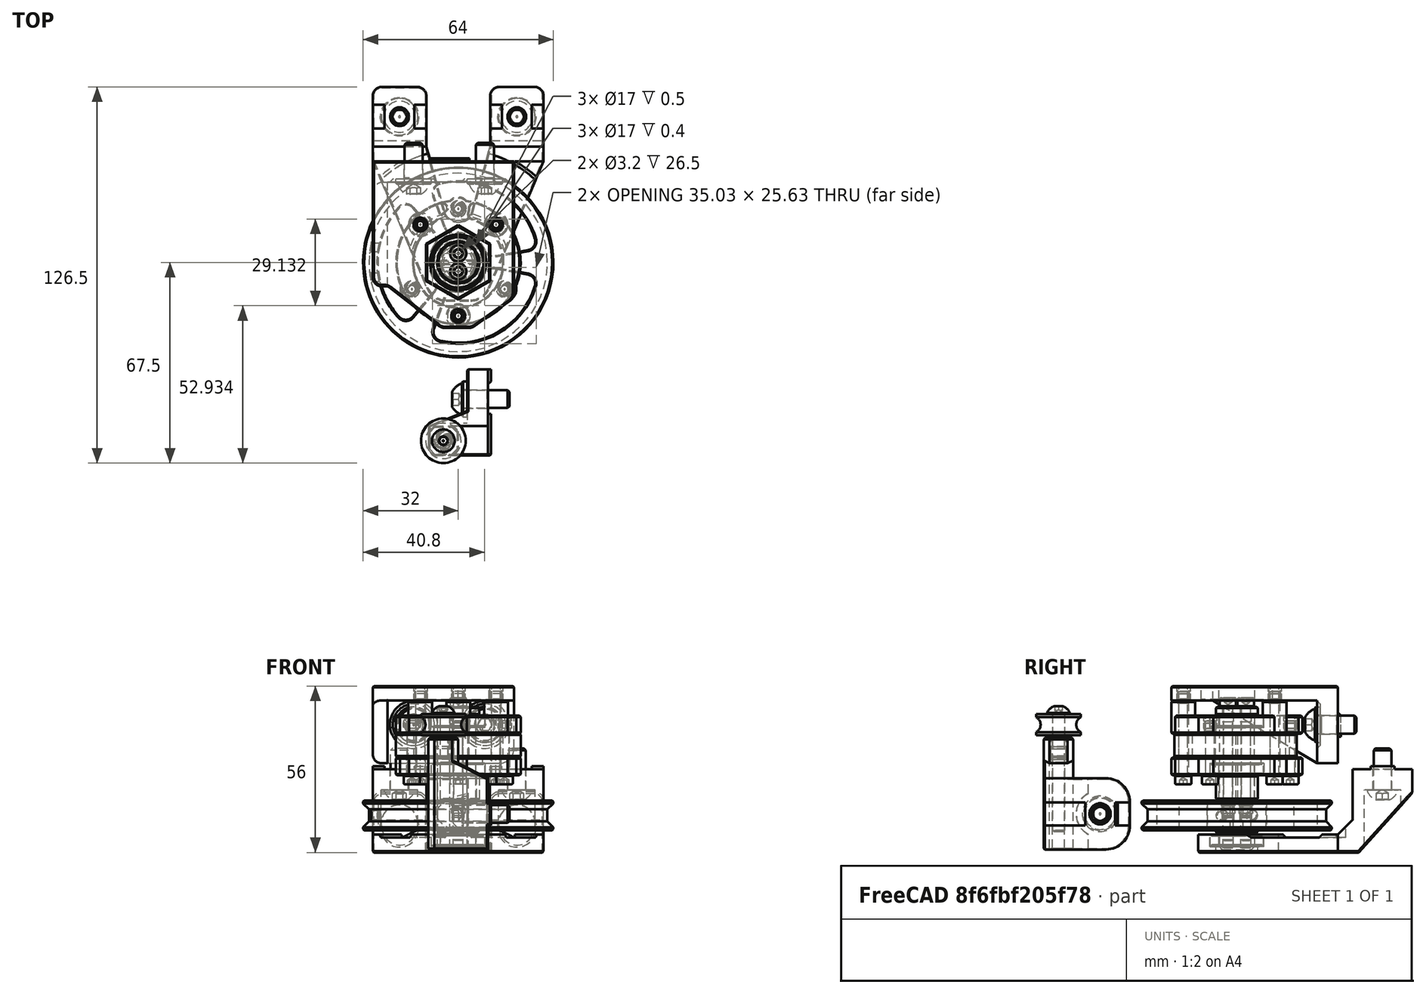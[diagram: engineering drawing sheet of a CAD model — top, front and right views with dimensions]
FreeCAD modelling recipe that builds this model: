
FCSTD DOCUMENT  (FreeCAD 0.19R24291 (Git))
Label: counter-weight-spring-box-assembly
License: Other
LicenseURL: GPL3
objects: Part::FeaturePython×26, Part::Feature×15, PartDesign::CoordinateSystem×2, App::Part×2
note: 43 computed .brp shape members not serialized (recipe doc carries the construction recipe); baked Part::Feature solids carry a one-line shape summary decoded from their .brp

FEATURE [Part::Feature] Chamfer001001  label="bearing-6701ZZ1"
  Placement = pos=(0,0,-2) rot=(0,0,1;0rad)
  shape: bbox 18 x 18 x 4 mm, 20 faces (baked)
FEATURE [Part::Feature] Body001001001002003011001005  label="cw-mid-plate"
  Placement = pos=(0,0,-2) rot=(0,0,1;0rad)
  shape: bbox 42 x 41.91 x 12.4 mm, 62 faces (baked)
FEATURE [Part::Feature] Body003002  label="cw-axis"
  Placement = pos=(0,0,21) rot=(0.707107,-0.707107,0;3.14159rad)
  shape: bbox 14.1 x 14.1 x 31.5 mm, 25 faces (baked)
FEATURE [Part::Feature] Body001001001002003011001002001  label="cw-front-plate"
  Placement = pos=(0,0,-2) rot=(0,0,1;0rad)
  shape: bbox 42 x 44 x 6 mm, 67 faces (baked)
FEATURE [Part::Feature] Body001001001002003011001003001  label="cw-back-plate"
  Placement = pos=(0,0,-2) rot=(0,0,1;0rad)
  shape: bbox 42 x 44 x 11 mm, 69 faces (baked)
FEATURE [Part::Feature] Chamfer003068012002063001  label="bearing-6701ZZ2"
  Placement = pos=(0,0,14) rot=(0,0,1;0rad)
  shape: bbox 18 x 18 x 4 mm, 20 faces (baked)
FEATURE [Part::Feature] Body001001001002003011001004001  label="cw-spacer"
  Placement = pos=(0,0,-2) rot=(0,0,1;0rad)
  shape: bbox 14.1 x 14.1 x 8.35 mm, 6 faces (baked)
FEATURE [Part::Feature] Chamfer003068012002073001  label="bearing-6701ZZ"
  Placement = pos=(0,0,-26) rot=(0,0,1;0rad)
  shape: bbox 18 x 18 x 4 mm, 20 faces (baked)
FEATURE [Part::Feature] Chamfer003068012002090001  label="cw-front-mounter"
  shape: bbox 57.46 x 72 x 29 mm, 102 faces (baked)
FEATURE [Part::Feature] Chamfer003068012002102001  label="cw-back-mounter"
  Placement = pos=(0,0,-20) rot=(0,0,1;0rad)
  shape: bbox 47.46 x 57 x 26 mm, 78 faces (baked)
FEATURE [Part::Feature] Body001001001002003011001004002  label="cw-pulley-r30"
  Placement = pos=(1e-15,0,-10.5) rot=(0,1,0;3.14159rad)
  shape: bbox 64 x 64 x 16.5 mm, 104 faces (baked)
FEATURE [Part::FeaturePython] HeatSet  label="M3x4-HeatSet"  # WARN: FeaturePython — macro-defined, semantics opaque (R4)
  Placement = pos=(-12.7279,12.7279,28) rot=(0,0,1;0rad)
  baseObject = -> Chamfer003068012002102001 [Edge160]
  diameter = 2
  invert = false
  leftHanded = false
  offset = 0
FEATURE [Part::FeaturePython] HeatSet001  label="M3x4-HeatSet001"  # WARN: FeaturePython — macro-defined, semantics opaque (R4)
  Placement = pos=(0,-18,28) rot=(0,0,1;0rad)
  baseObject = -> Chamfer003068012002102001 [Edge162]
  diameter = 2
  invert = false
  leftHanded = false
  offset = 0
FEATURE [Part::FeaturePython] HeatSet002  label="M3x4-HeatSet002"  # WARN: FeaturePython — macro-defined, semantics opaque (R4)
  Placement = pos=(12.7279,12.7279,28) rot=(0,0,1;0rad)
  baseObject = -> Chamfer003068012002102001 [Edge161]
  diameter = 2
  invert = false
  leftHanded = false
  offset = 0
FEATURE [Part::FeaturePython] HeatSet004  label="M3x4-HeatSet003"  # WARN: FeaturePython — macro-defined, semantics opaque (R4)
  Placement = pos=(15.5885,-9,18) rot=(0,0,1;0rad)
  baseObject = -> Body001001001002003011001003001 [Edge19]
  diameter = 2
  invert = false
  leftHanded = false
  offset = 0
FEATURE [Part::FeaturePython] HeatSet005  label="M3x4-HeatSet004"  # WARN: FeaturePython — macro-defined, semantics opaque (R4)
  Placement = pos=(-15.5885,-9,18) rot=(0,0,1;0rad)
  baseObject = -> Body001001001002003011001003001 [Edge17]
  diameter = 2
  invert = false
  leftHanded = false
  offset = 0
FEATURE [Part::FeaturePython] HeatSet006  label="M3x4-HeatSet005"  # WARN: FeaturePython — macro-defined, semantics opaque (R4)
  Placement = pos=(1.1e-15,18,18) rot=(0,0,1;0rad)
  baseObject = -> Body001001001002003011001003001 [Edge20]
  diameter = 2
  invert = false
  leftHanded = false
  offset = 0
FEATURE [Part::FeaturePython] HeatSet007  label="M3x4-HeatSet006"  # WARN: FeaturePython — macro-defined, semantics opaque (R4)
  Placement = pos=(0,-3,-10.5) rot=(0,0,1;0rad)
  baseObject = -> Body001001001002003011001004002 [Edge68]
  diameter = 2
  invert = false
  leftHanded = false
  offset = 0
FEATURE [Part::FeaturePython] HeatSet008  label="M3x4-HeatSet007"  # WARN: FeaturePython — macro-defined, semantics opaque (R4)
  Placement = pos=(2e-15,3,-10.5) rot=(0,0,1;0rad)
  baseObject = -> Body001001001002003011001004002 [Edge69]
  diameter = 2
  invert = false
  leftHanded = false
  offset = 0
FEATURE [Part::FeaturePython] Screw  label="M3x20-Screw"  # Fasteners workbench fastener (typed FeaturePython)
  Placement = pos=(15.5885,-9,-2) rot=(1,0,0;3.14159rad)
  baseObject = -> Body001001001002003011001002001 [Edge49]
  diameter = 4
  invert = false
  leftHanded = false
  length = 7
  lengthCustom = 20
  matchOuter = true
  offset = 0
  thread = false
  type = 34
FEATURE [Part::FeaturePython] Screw001  label="M3x20-Screw003"  # Fasteners workbench fastener (typed FeaturePython)
  Placement = pos=(-15.5885,-9,-2) rot=(1,0,0;3.14159rad)
  baseObject = -> Body001001001002003011001002001 [Edge48]
  diameter = 4
  invert = false
  leftHanded = false
  length = 7
  lengthCustom = 20
  matchOuter = true
  offset = 0
  thread = false
  type = 34
FEATURE [Part::FeaturePython] Screw002  label="M3x20-Screw004"  # Fasteners workbench fastener (typed FeaturePython)
  Placement = pos=(1e-15,18,-2) rot=(1,0,0;3.14159rad)
  baseObject = -> Body001001001002003011001002001 [Edge51]
  diameter = 4
  invert = false
  leftHanded = false
  length = 7
  lengthCustom = 20
  matchOuter = true
  offset = 0
  thread = false
  type = 34
FEATURE [Part::FeaturePython] Screw003  label="M3x30-Screw"  # Fasteners workbench fastener (typed FeaturePython)
  Placement = pos=(12.7279,12.7279,-2) rot=(1,0,0;3.14159rad)
  baseObject = -> Body001001001002003011001002001 [Edge47]
  diameter = 4
  invert = false
  leftHanded = false
  length = 9
  lengthCustom = 30
  matchOuter = true
  offset = 0
  thread = false
  type = 34
FEATURE [Part::FeaturePython] Screw004  label="M3x30-Screw003"  # Fasteners workbench fastener (typed FeaturePython)
  Placement = pos=(-12.7279,12.7279,-2) rot=(1,0,0;3.14159rad)
  baseObject = -> Body001001001002003011001002001 [Edge46]
  diameter = 4
  invert = false
  leftHanded = false
  length = 9
  lengthCustom = 30
  matchOuter = true
  offset = 0
  thread = false
  type = 34
FEATURE [Part::FeaturePython] Screw005  label="M3x30-Screw004"  # Fasteners workbench fastener (typed FeaturePython)
  Placement = pos=(-1.2155e-11,-18,-2) rot=(1,0,0;3.14159rad)
  baseObject = -> Body001001001002003011001002001 [Edge50]
  diameter = 4
  invert = false
  leftHanded = false
  length = 9
  lengthCustom = 30
  matchOuter = true
  offset = 0
  thread = false
  type = 34
FEATURE [Part::FeaturePython] Screw006  label="M3x45-Screw"  # Fasteners workbench fastener (typed FeaturePython)
  Placement = pos=(-1e-15,3,21) rot=(0,0,1;0rad)
  baseObject = -> Body003002 [Edge7]
  diameter = 4
  invert = true
  leftHanded = false
  length = 10
  lengthCustom = 45
  matchOuter = true
  offset = 0
  thread = false
  type = 34
FEATURE [Part::FeaturePython] Screw007  label="M3x45-Screw001"  # Fasteners workbench fastener (typed FeaturePython)
  Placement = pos=(1e-15,-3,21) rot=(0,0,1;0rad)
  baseObject = -> Body003002 [Edge8]
  diameter = 4
  invert = true
  leftHanded = false
  length = 10
  lengthCustom = 45
  matchOuter = true
  offset = 0
  thread = false
  type = 34
FEATURE [Part::FeaturePython] Washer  label="M6-Washer"  # Fasteners workbench fastener (typed FeaturePython)
  Placement = pos=(9,28,15) rot=(1,0,0;1.5708rad)
  baseObject = -> Chamfer003068012002102001 [Edge163]
  diameter = 2
  invert = true
  leftHanded = false
  matchOuter = true
  offset = 0
  type = 4
FEATURE [Part::FeaturePython] Washer001  label="M6-Washer001"  # Fasteners workbench fastener (typed FeaturePython)
  Placement = pos=(-15,28,15) rot=(1,0,0;1.5708rad)
  baseObject = -> Chamfer003068012002102001 [Edge97]
  diameter = 2
  invert = true
  leftHanded = false
  matchOuter = true
  offset = 0
  type = 4
FEATURE [Part::FeaturePython] Screw008  label="M6x14-Screw"  # Fasteners workbench fastener (typed FeaturePython)
  Placement = pos=(9,26.2,15) rot=(1,0,0;1.5708rad)
  baseObject = -> Washer [Edge1]
  diameter = 4
  invert = false
  leftHanded = false
  length = 2
  lengthCustom = 14
  matchOuter = true
  offset = 0
  thread = false
  type = 40
FEATURE [Part::FeaturePython] Screw009  label="M6x14-Screw001"  # Fasteners workbench fastener (typed FeaturePython)
  Placement = pos=(-15,26.2,15) rot=(1,0,0;1.5708rad)
  baseObject = -> Washer001 [Edge1]
  diameter = 4
  invert = false
  leftHanded = false
  length = 2
  lengthCustom = 14
  matchOuter = true
  offset = 0
  thread = false
  type = 40
FEATURE [Part::FeaturePython] Screw010  label="M6x14-Screw002"  # Fasteners workbench fastener (typed FeaturePython)
  Placement = pos=(-19.73,49,-7) rot=(1,0,0;3.14159rad)
  baseObject = -> Chamfer003068012002090001 [Edge194]
  diameter = 4
  invert = true
  leftHanded = false
  length = 2
  lengthCustom = 14
  matchOuter = true
  offset = 0
  thread = false
  type = 40
FEATURE [Part::FeaturePython] Screw011  label="M6x14-Screw003"  # Fasteners workbench fastener (typed FeaturePython)
  Placement = pos=(19.73,49,-7) rot=(1,0,0;3.14159rad)
  baseObject = -> Chamfer003068012002090001 [Edge254]
  diameter = 4
  invert = true
  leftHanded = false
  length = 2
  lengthCustom = 14
  matchOuter = true
  offset = 0
  thread = false
  type = 40
FEATURE [PartDesign::CoordinateSystem] LCS_counter_spring_box  label="LCS_counter-spring-box"
  AttacherType = Attacher::AttachEngine3D
FEATURE [App::Part] Part  label="counter-weight-sprintg-box"
  Group = -> [Body001001001002003011001004002,Chamfer001001,Body001001001002003011001005,Body003002,Body001001001002003011001002001,Body001001001002003011001003001,Chamfer003068012002063001,Body001001001002003011001004001,Chamfer003068012002073001,Chamfer003068012002090001,Chamfer003068012002102001,HeatSet,HeatSet001,HeatSet002,HeatSet004,HeatSet005,HeatSet006,HeatSet007,HeatSet008,Screw,Screw001,Screw002,+12 more]
  Origin = -> Origin
FEATURE [Part::Feature] Body001001001002003006001  label="counter-weight-top-arm001"
  Placement = pos=(10,-25,0) rot=(0,0,1;0rad)
  shape: bbox 21 x 29 x 37.5 mm, 69 faces (baked)
FEATURE [Part::Feature] Body001001001002003005  label="U624ZZ-bearing"
  Placement = pos=(-5,-60,15) rot=(0,1,0;1.5708rad)
  shape: bbox 15 x 15 x 7 mm, 6 faces (baked)
FEATURE [Part::Feature] Cut001021001  label="spacer-0p5mm"
  Placement = pos=(-5,-60,18.5) rot=(0,0,1;0rad)
  shape: bbox 6.3 x 6.3 x 0.5 mm, 4 faces (baked)
FEATURE [Part::Feature] Cut001020001  label="spacer-1mm"
  Placement = pos=(-5,-60,10.5) rot=(0,0,1;0rad)
  shape: bbox 6.3 x 6.3 x 1 mm, 4 faces (baked)
FEATURE [Part::FeaturePython] Screw012  label="M4x40-Screw"  # Fasteners workbench fastener (typed FeaturePython)
  Placement = pos=(-5,-60,19) rot=(0,0,1;0rad)
  baseObject = -> Cut001021001 [Edge4]
  diameter = 2
  invert = false
  leftHanded = false
  length = 10
  lengthCustom = 40
  matchOuter = true
  offset = 0
  thread = false
  type = 40
FEATURE [Part::FeaturePython] HeatSet009  label="M4-HeatSet"  # WARN: FeaturePython — macro-defined, semantics opaque (R4)
  Placement = pos=(-5,-60,10.5) rot=(0,0,1;0rad)
  baseObject = -> Body001001001002003006001 [Edge40]
  diameter = 4
  invert = false
  leftHanded = false
  offset = 0
FEATURE [Part::FeaturePython] Washer002  label="M6-Washer002"  # Fasteners workbench fastener (typed FeaturePython)
  Placement = pos=(3,-46,-15) rot=(0,-1,0;1.5708rad)
  baseObject = -> Body001001001002003006001 [Edge132]
  diameter = 2
  invert = true
  leftHanded = false
  matchOuter = true
  offset = 0
  type = 4
FEATURE [Part::FeaturePython] Screw013  label="M6x16-Screw"  # Fasteners workbench fastener (typed FeaturePython)
  Placement = pos=(1.2,-46,-15) rot=(0,-1,0;1.5708rad)
  baseObject = -> Washer002 [Edge1]
  diameter = 4
  invert = false
  leftHanded = false
  length = 3
  lengthCustom = 16
  matchOuter = true
  offset = 0
  thread = false
  type = 40
FEATURE [PartDesign::CoordinateSystem] LCS_counter_weight_top_arm  label="LCS_counter-weight-top-arm"
  AttacherType = Attacher::AttachEngine3D
FEATURE [App::Part] Part001  label="counter-weight-top-arm"
  Group = -> [Body001001001002003006001,Body001001001002003005,Cut001021001,Cut001020001,Screw012,HeatSet009,Washer002,Screw013,LCS_counter_weight_top_arm]
  Origin = -> Origin001
